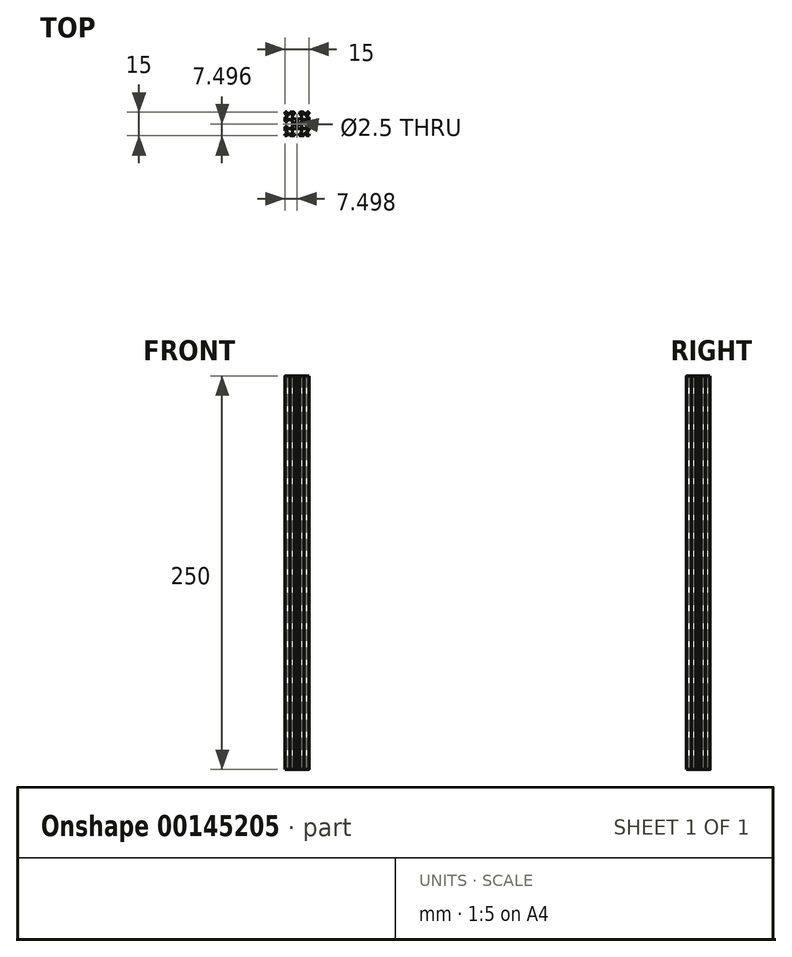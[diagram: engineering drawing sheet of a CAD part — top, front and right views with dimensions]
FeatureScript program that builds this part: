
annotation { "Feature Type Name" : "Feature", "Feature Type Description" : "" }
export const myFeature = defineFeature(function(context is Context, id is Id, definition is map)
    precondition{}
    {
        {
            var Q0;
            Q0=qCreatedBy(makeId("Top.planeOp"),FACE);
            var sketch = newSketch(context, id + "F0", { "sketchPlane" : qUnion([Q0])});
            skCircle(sketch, "E0", {"center": v(-4.16, 17.74) * mm, "radius": 1.25 * mm});
            skArc(sketch, "E1", {"start": v(-3.34, 15.19) * mm, "mid": v(-3.4, 15.33) * mm, "end": v(-3.54, 15.39) * mm});
            skLineSegment(sketch, "E2", {"start": v(-3.54, 15.39) * mm, "end": v(-4.79, 15.39) * mm});
            skArc(sketch, "E3", {"start": v(-4.79, 15.39) * mm, "mid": v(-4.93, 15.33) * mm, "end": v(-4.99, 15.19) * mm});
            skLineSegment(sketch, "E4", {"start": v(-4.99, 15.19) * mm, "end": v(-4.99, 14.96) * mm});
            skArc(sketch, "E5", {"start": v(-5.14, 14.77) * mm, "mid": v(-5.03, 14.84) * mm, "end": v(-4.99, 14.96) * mm});
            skLineSegment(sketch, "E6", {"start": v(-5.14, 14.77) * mm, "end": v(-6.67, 14.42) * mm});
            skArc(sketch, "E7", {"start": v(-6.67, 14.42) * mm, "mid": v(-6.95, 14.25) * mm, "end": v(-7.06, 13.94) * mm});
            skLineSegment(sketch, "E8", {"start": v(-7.06, 13.94) * mm, "end": v(-7.06, 11.84) * mm});
            skArc(sketch, "E9", {"start": v(-7.06, 11.84) * mm, "mid": v(-7, 11.7) * mm, "end": v(-6.86, 11.64) * mm});
            skLineSegment(sketch, "E10", {"start": v(-6.86, 11.64) * mm, "end": v(-6.26, 11.64) * mm});
            skArc(sketch, "E11", {"start": v(-5.76, 11.14) * mm, "mid": v(-5.9, 11.49) * mm, "end": v(-6.26, 11.64) * mm});
            skLineSegment(sketch, "E12", {"start": v(-5.76, 11.14) * mm, "end": v(-5.76, 10.74) * mm});
            skArc(sketch, "E13", {"start": v(-6.26, 10.24) * mm, "mid": v(-5.9, 10.38) * mm, "end": v(-5.76, 10.74) * mm});
            skArc(sketch, "E14", {"start": v(-8.56, 10.74) * mm, "mid": v(-8.42, 10.38) * mm, "end": v(-8.06, 10.24) * mm});
            skLineSegment(sketch, "E15", {"start": v(-8.56, 10.74) * mm, "end": v(-8.56, 11.07) * mm});
            skArc(sketch, "E16", {"start": v(-8.56, 11.07) * mm, "mid": v(-8.87, 11.53) * mm, "end": v(-9.42, 11.42) * mm});
            skLineSegment(sketch, "E17", {"start": v(-9.42, 11.42) * mm, "end": v(-10.45, 10.38) * mm});
            skArc(sketch, "E18", {"start": v(-10.8, 10.24) * mm, "mid": v(-10.62, 10.27) * mm, "end": v(-10.45, 10.38) * mm});
            skArc(sketch, "E19", {"start": v(-11.66, 10.49) * mm, "mid": v(-11.59, 10.3) * mm, "end": v(-11.41, 10.24) * mm});
            skArc(sketch, "E20", {"start": v(-11.52, 11.44) * mm, "mid": v(-11.62, 11.28) * mm, "end": v(-11.66, 11.09) * mm});
            skLineSegment(sketch, "E21", {"start": v(-11.52, 11.44) * mm, "end": v(-10.48, 12.48) * mm});
            skArc(sketch, "E22", {"start": v(-10.48, 12.48) * mm, "mid": v(-10.37, 13.03) * mm, "end": v(-10.83, 13.34) * mm});
            skLineSegment(sketch, "E23", {"start": v(-10.83, 13.34) * mm, "end": v(-11.16, 13.34) * mm});
            skArc(sketch, "E24", {"start": v(-11.66, 13.84) * mm, "mid": v(-11.52, 13.48) * mm, "end": v(-11.16, 13.34) * mm});
            skLineSegment(sketch, "E25", {"start": v(-11.66, 15.64) * mm, "end": v(-11.66, 13.84) * mm});
            skArc(sketch, "E26", {"start": v(-11.16, 16.14) * mm, "mid": v(-11.52, 15.99) * mm, "end": v(-11.66, 15.64) * mm});
            skLineSegment(sketch, "E27", {"start": v(-11.16, 16.14) * mm, "end": v(-10.76, 16.14) * mm});
            skArc(sketch, "E28", {"start": v(-10.26, 15.64) * mm, "mid": v(-10.4, 15.99) * mm, "end": v(-10.76, 16.14) * mm});
            skLineSegment(sketch, "E29", {"start": v(-10.26, 15.64) * mm, "end": v(-10.26, 15.04) * mm});
            skArc(sketch, "E30", {"start": v(-10.26, 15.04) * mm, "mid": v(-10.2, 14.9) * mm, "end": v(-10.06, 14.84) * mm});
            skLineSegment(sketch, "E31", {"start": v(-10.06, 14.84) * mm, "end": v(-7.96, 14.84) * mm});
            skArc(sketch, "E32", {"start": v(-7.96, 14.84) * mm, "mid": v(-7.65, 14.95) * mm, "end": v(-7.47, 15.23) * mm});
            skLineSegment(sketch, "E33", {"start": v(-7.47, 15.23) * mm, "end": v(-7.13, 16.75) * mm});
            skArc(sketch, "E34", {"start": v(-6.94, 16.91) * mm, "mid": v(-7.06, 16.87) * mm, "end": v(-7.13, 16.75) * mm});
            skLineSegment(sketch, "E35", {"start": v(-6.94, 16.91) * mm, "end": v(-6.7, 16.91) * mm});
            skArc(sketch, "E36", {"start": v(-6.7, 16.91) * mm, "mid": v(-6.57, 16.97) * mm, "end": v(-6.5, 17.11) * mm});
            skLineSegment(sketch, "E37", {"start": v(-6.5, 17.11) * mm, "end": v(-6.5, 18.36) * mm});
            skArc(sketch, "E38", {"start": v(-6.5, 18.36) * mm, "mid": v(-6.57, 18.5) * mm, "end": v(-6.7, 18.56) * mm});
            skLineSegment(sketch, "E39", {"start": v(-6.7, 18.56) * mm, "end": v(-6.94, 18.56) * mm});
            skArc(sketch, "E40", {"start": v(-7.13, 18.72) * mm, "mid": v(-7.06, 18.6) * mm, "end": v(-6.94, 18.56) * mm});
            skLineSegment(sketch, "E41", {"start": v(-7.13, 18.72) * mm, "end": v(-7.47, 20.25) * mm});
            skArc(sketch, "E42", {"start": v(-7.47, 20.25) * mm, "mid": v(-7.65, 20.53) * mm, "end": v(-7.96, 20.64) * mm});
            skLineSegment(sketch, "E43", {"start": v(-7.96, 20.64) * mm, "end": v(-10.06, 20.64) * mm});
            skArc(sketch, "E44", {"start": v(-10.06, 20.64) * mm, "mid": v(-10.2, 20.58) * mm, "end": v(-10.26, 20.44) * mm});
            skLineSegment(sketch, "E45", {"start": v(-10.26, 20.44) * mm, "end": v(-10.26, 19.84) * mm});
            skArc(sketch, "E46", {"start": v(-10.76, 19.34) * mm, "mid": v(-10.4, 19.48) * mm, "end": v(-10.26, 19.84) * mm});
            skLineSegment(sketch, "E47", {"start": v(-10.76, 19.34) * mm, "end": v(-11.16, 19.34) * mm});
            skArc(sketch, "E48", {"start": v(-11.66, 19.84) * mm, "mid": v(-11.52, 19.48) * mm, "end": v(-11.16, 19.34) * mm});
            skArc(sketch, "E49", {"start": v(-11.16, 22.14) * mm, "mid": v(-11.52, 21.99) * mm, "end": v(-11.66, 21.64) * mm});
            skLineSegment(sketch, "E50", {"start": v(-11.16, 22.14) * mm, "end": v(-10.83, 22.14) * mm});
            skArc(sketch, "E51", {"start": v(-10.83, 22.14) * mm, "mid": v(-10.37, 22.44) * mm, "end": v(-10.48, 22.99) * mm});
            skLineSegment(sketch, "E52", {"start": v(-10.48, 22.99) * mm, "end": v(-11.52, 24.03) * mm});
            skArc(sketch, "E53", {"start": v(-11.66, 24.38) * mm, "mid": v(-11.62, 24.2) * mm, "end": v(-11.52, 24.03) * mm});
            skArc(sketch, "E54", {"start": v(-11.41, 25.24) * mm, "mid": v(-11.59, 25.16) * mm, "end": v(-11.66, 24.99) * mm});
            skArc(sketch, "E55", {"start": v(-10.45, 25.09) * mm, "mid": v(-10.62, 25.2) * mm, "end": v(-10.8, 25.24) * mm});
            skLineSegment(sketch, "E56", {"start": v(-10.45, 25.09) * mm, "end": v(-9.42, 24.05) * mm});
            skArc(sketch, "E57", {"start": v(-9.42, 24.05) * mm, "mid": v(-8.87, 23.94) * mm, "end": v(-8.56, 24.4) * mm});
            skLineSegment(sketch, "E58", {"start": v(-8.56, 24.4) * mm, "end": v(-8.56, 24.74) * mm});
            skArc(sketch, "E59", {"start": v(-8.06, 25.24) * mm, "mid": v(-8.42, 25.09) * mm, "end": v(-8.56, 24.74) * mm});
            skArc(sketch, "E60", {"start": v(-5.76, 24.74) * mm, "mid": v(-5.9, 25.09) * mm, "end": v(-6.26, 25.24) * mm});
            skLineSegment(sketch, "E61", {"start": v(-5.76, 24.74) * mm, "end": v(-5.76, 24.34) * mm});
            skArc(sketch, "E62", {"start": v(-6.26, 23.84) * mm, "mid": v(-5.9, 23.98) * mm, "end": v(-5.76, 24.34) * mm});
            skLineSegment(sketch, "E63", {"start": v(-6.26, 23.84) * mm, "end": v(-6.86, 23.84) * mm});
            skArc(sketch, "E64", {"start": v(-6.86, 23.84) * mm, "mid": v(-7, 23.78) * mm, "end": v(-7.06, 23.64) * mm});
            skLineSegment(sketch, "E65", {"start": v(-7.06, 23.64) * mm, "end": v(-7.06, 21.54) * mm});
            skArc(sketch, "E66", {"start": v(-7.06, 21.54) * mm, "mid": v(-6.95, 21.22) * mm, "end": v(-6.67, 21.05) * mm});
            skLineSegment(sketch, "E67", {"start": v(-6.67, 21.05) * mm, "end": v(-5.14, 20.7) * mm});
            skArc(sketch, "E68", {"start": v(-4.99, 20.51) * mm, "mid": v(-5.03, 20.64) * mm, "end": v(-5.14, 20.7) * mm});
            skLineSegment(sketch, "E69", {"start": v(-4.99, 20.51) * mm, "end": v(-4.99, 20.28) * mm});
            skArc(sketch, "E70", {"start": v(-4.99, 20.28) * mm, "mid": v(-4.93, 20.14) * mm, "end": v(-4.79, 20.08) * mm});
            skLineSegment(sketch, "E71", {"start": v(-4.79, 20.08) * mm, "end": v(-3.54, 20.08) * mm});
            skArc(sketch, "E72", {"start": v(-3.54, 20.08) * mm, "mid": v(-3.4, 20.14) * mm, "end": v(-3.34, 20.28) * mm});
            skLineSegment(sketch, "E73", {"start": v(-3.34, 20.28) * mm, "end": v(-3.34, 20.51) * mm});
            skArc(sketch, "E74", {"start": v(-3.18, 20.7) * mm, "mid": v(-3.3, 20.64) * mm, "end": v(-3.34, 20.51) * mm});
            skLineSegment(sketch, "E75", {"start": v(-3.18, 20.7) * mm, "end": v(-1.65, 21.05) * mm});
            skArc(sketch, "E76", {"start": v(-1.65, 21.05) * mm, "mid": v(-1.37, 21.22) * mm, "end": v(-1.26, 21.54) * mm});
            skLineSegment(sketch, "E77", {"start": v(-1.26, 21.54) * mm, "end": v(-1.26, 23.64) * mm});
            skArc(sketch, "E78", {"start": v(-1.26, 23.64) * mm, "mid": v(-1.32, 23.78) * mm, "end": v(-1.46, 23.84) * mm});
            skLineSegment(sketch, "E79", {"start": v(-1.46, 23.84) * mm, "end": v(-2.06, 23.84) * mm});
            skArc(sketch, "E80", {"start": v(-2.56, 24.34) * mm, "mid": v(-2.42, 23.98) * mm, "end": v(-2.06, 23.84) * mm});
            skLineSegment(sketch, "E81", {"start": v(-2.56, 24.34) * mm, "end": v(-2.56, 24.74) * mm});
            skArc(sketch, "E82", {"start": v(-2.06, 25.24) * mm, "mid": v(-2.42, 25.09) * mm, "end": v(-2.56, 24.74) * mm});
            skArc(sketch, "E83", {"start": v(0.24, 24.74) * mm, "mid": v(0.1, 25.09) * mm, "end": v(-0.26, 25.24) * mm});
            skLineSegment(sketch, "E84", {"start": v(0.24, 24.74) * mm, "end": v(0.24, 24.4) * mm});
            skArc(sketch, "E85", {"start": v(0.24, 24.4) * mm, "mid": v(0.55, 23.94) * mm, "end": v(1.1, 24.05) * mm});
            skLineSegment(sketch, "E86", {"start": v(1.1, 24.05) * mm, "end": v(2.13, 25.09) * mm});
            skArc(sketch, "E87", {"start": v(2.48, 25.24) * mm, "mid": v(2.3, 25.2) * mm, "end": v(2.13, 25.09) * mm});
            skLineSegment(sketch, "E88", {"start": v(3.09, 25.24) * mm, "end": v(2.48, 25.24) * mm});
            skArc(sketch, "E89", {"start": v(3.34, 24.99) * mm, "mid": v(3.27, 25.16) * mm, "end": v(3.09, 25.24) * mm});
            skArc(sketch, "E90", {"start": v(3.2, 24.03) * mm, "mid": v(3.3, 24.2) * mm, "end": v(3.34, 24.38) * mm});
            skLineSegment(sketch, "E91", {"start": v(3.2, 24.03) * mm, "end": v(2.15, 22.99) * mm});
            skArc(sketch, "E92", {"start": v(2.15, 22.99) * mm, "mid": v(2.04, 22.44) * mm, "end": v(2.5, 22.14) * mm});
            skLineSegment(sketch, "E93", {"start": v(2.5, 22.14) * mm, "end": v(2.84, 22.14) * mm});
            skArc(sketch, "E94", {"start": v(3.34, 21.64) * mm, "mid": v(3.2, 21.99) * mm, "end": v(2.84, 22.14) * mm});
            skArc(sketch, "E95", {"start": v(2.84, 19.34) * mm, "mid": v(3.2, 19.48) * mm, "end": v(3.34, 19.84) * mm});
            skLineSegment(sketch, "E96", {"start": v(2.84, 19.34) * mm, "end": v(2.44, 19.34) * mm});
            skArc(sketch, "E97", {"start": v(1.94, 19.84) * mm, "mid": v(2.08, 19.48) * mm, "end": v(2.44, 19.34) * mm});
            skLineSegment(sketch, "E98", {"start": v(1.94, 19.84) * mm, "end": v(1.94, 20.44) * mm});
            skArc(sketch, "E99", {"start": v(1.94, 20.44) * mm, "mid": v(1.88, 20.58) * mm, "end": v(1.74, 20.64) * mm});
            skLineSegment(sketch, "E100", {"start": v(1.74, 20.64) * mm, "end": v(-0.36, 20.64) * mm});
            skArc(sketch, "E101", {"start": v(-0.36, 20.64) * mm, "mid": v(-0.67, 20.53) * mm, "end": v(-0.85, 20.25) * mm});
            skLineSegment(sketch, "E102", {"start": v(-0.85, 20.25) * mm, "end": v(-1.2, 18.72) * mm});
            skArc(sketch, "E103", {"start": v(-1.39, 18.56) * mm, "mid": v(-1.26, 18.6) * mm, "end": v(-1.2, 18.72) * mm});
            skLineSegment(sketch, "E104", {"start": v(-1.39, 18.56) * mm, "end": v(-1.61, 18.56) * mm});
            skArc(sketch, "E105", {"start": v(-1.61, 18.56) * mm, "mid": v(-1.76, 18.5) * mm, "end": v(-1.81, 18.36) * mm});
            skLineSegment(sketch, "E106", {"start": v(-1.81, 18.36) * mm, "end": v(-1.81, 17.11) * mm});
            skArc(sketch, "E107", {"start": v(-1.81, 17.11) * mm, "mid": v(-1.76, 16.97) * mm, "end": v(-1.61, 16.91) * mm});
            skLineSegment(sketch, "E108", {"start": v(-1.61, 16.91) * mm, "end": v(-1.39, 16.91) * mm});
            skArc(sketch, "E109", {"start": v(-1.2, 16.75) * mm, "mid": v(-1.26, 16.87) * mm, "end": v(-1.39, 16.91) * mm});
            skLineSegment(sketch, "E110", {"start": v(-1.2, 16.75) * mm, "end": v(-0.85, 15.23) * mm});
            skArc(sketch, "E111", {"start": v(-0.85, 15.23) * mm, "mid": v(-0.67, 14.95) * mm, "end": v(-0.36, 14.84) * mm});
            skLineSegment(sketch, "E112", {"start": v(-0.36, 14.84) * mm, "end": v(1.74, 14.84) * mm});
            skArc(sketch, "E113", {"start": v(1.74, 14.84) * mm, "mid": v(1.88, 14.9) * mm, "end": v(1.94, 15.04) * mm});
            skLineSegment(sketch, "E114", {"start": v(1.94, 15.04) * mm, "end": v(1.94, 15.64) * mm});
            skArc(sketch, "E115", {"start": v(2.44, 16.14) * mm, "mid": v(2.08, 15.99) * mm, "end": v(1.94, 15.64) * mm});
            skLineSegment(sketch, "E116", {"start": v(2.44, 16.14) * mm, "end": v(2.84, 16.14) * mm});
            skArc(sketch, "E117", {"start": v(3.34, 15.64) * mm, "mid": v(3.2, 15.99) * mm, "end": v(2.84, 16.14) * mm});
            skLineSegment(sketch, "E118", {"start": v(3.34, 13.84) * mm, "end": v(3.34, 15.64) * mm});
            skArc(sketch, "E119", {"start": v(2.84, 13.34) * mm, "mid": v(3.2, 13.48) * mm, "end": v(3.34, 13.84) * mm});
            skLineSegment(sketch, "E120", {"start": v(2.84, 13.34) * mm, "end": v(2.5, 13.34) * mm});
            skArc(sketch, "E121", {"start": v(2.5, 13.34) * mm, "mid": v(2.04, 13.03) * mm, "end": v(2.15, 12.48) * mm});
            skLineSegment(sketch, "E122", {"start": v(2.15, 12.48) * mm, "end": v(3.2, 11.44) * mm});
            skArc(sketch, "E123", {"start": v(3.34, 11.09) * mm, "mid": v(3.3, 11.28) * mm, "end": v(3.2, 11.44) * mm});
            skArc(sketch, "E124", {"start": v(3.09, 10.24) * mm, "mid": v(3.27, 10.3) * mm, "end": v(3.34, 10.49) * mm});
            skLineSegment(sketch, "E125", {"start": v(2.48, 10.24) * mm, "end": v(3.09, 10.24) * mm});
            skArc(sketch, "E126", {"start": v(2.13, 10.38) * mm, "mid": v(2.3, 10.27) * mm, "end": v(2.48, 10.24) * mm});
            skLineSegment(sketch, "E127", {"start": v(2.13, 10.38) * mm, "end": v(1.1, 11.42) * mm});
            skArc(sketch, "E128", {"start": v(1.1, 11.42) * mm, "mid": v(0.55, 11.53) * mm, "end": v(0.24, 11.07) * mm});
            skLineSegment(sketch, "E129", {"start": v(0.24, 11.07) * mm, "end": v(0.24, 10.74) * mm});
            skArc(sketch, "E130", {"start": v(-0.26, 10.24) * mm, "mid": v(0.1, 10.38) * mm, "end": v(0.24, 10.74) * mm});
            skArc(sketch, "E131", {"start": v(-2.56, 10.74) * mm, "mid": v(-2.42, 10.38) * mm, "end": v(-2.06, 10.24) * mm});
            skLineSegment(sketch, "E132", {"start": v(-2.56, 10.74) * mm, "end": v(-2.56, 11.14) * mm});
            skArc(sketch, "E133", {"start": v(-2.06, 11.64) * mm, "mid": v(-2.42, 11.49) * mm, "end": v(-2.56, 11.14) * mm});
            skLineSegment(sketch, "E134", {"start": v(-2.06, 11.64) * mm, "end": v(-1.46, 11.64) * mm});
            skArc(sketch, "E135", {"start": v(-1.46, 11.64) * mm, "mid": v(-1.32, 11.7) * mm, "end": v(-1.26, 11.84) * mm});
            skLineSegment(sketch, "E136", {"start": v(-1.26, 11.84) * mm, "end": v(-1.26, 13.94) * mm});
            skArc(sketch, "E137", {"start": v(-1.26, 13.94) * mm, "mid": v(-1.37, 14.25) * mm, "end": v(-1.65, 14.42) * mm});
            skLineSegment(sketch, "E138", {"start": v(-1.65, 14.42) * mm, "end": v(-3.18, 14.77) * mm});
            skArc(sketch, "E139", {"start": v(-3.34, 14.96) * mm, "mid": v(-3.3, 14.84) * mm, "end": v(-3.18, 14.77) * mm});
            skLineSegment(sketch, "E140", {"start": v(-3.34, 14.96) * mm, "end": v(-3.34, 15.19) * mm});
            skLineSegment(sketch, "E141", {"start": v(-11.66, 21.64) * mm, "end": v(-11.66, 19.84) * mm});
            skLineSegment(sketch, "E142", {"start": v(-10.8, 25.24) * mm, "end": v(-11.41, 25.24) * mm});
            skLineSegment(sketch, "E143", {"start": v(-8.06, 10.24) * mm, "end": v(-6.26, 10.24) * mm});
            skLineSegment(sketch, "E144", {"start": v(3.34, 19.84) * mm, "end": v(3.34, 21.64) * mm});
            skLineSegment(sketch, "E145", {"start": v(-11.66, 24.99) * mm, "end": v(-11.66, 24.38) * mm});
            skLineSegment(sketch, "E146", {"start": v(3.34, 10.49) * mm, "end": v(3.34, 11.09) * mm});
            skLineSegment(sketch, "E147", {"start": v(3.34, 24.38) * mm, "end": v(3.34, 24.99) * mm});
            skLineSegment(sketch, "E148", {"start": v(-6.26, 25.24) * mm, "end": v(-8.06, 25.24) * mm});
            skLineSegment(sketch, "E149", {"start": v(-11.66, 11.09) * mm, "end": v(-11.66, 10.49) * mm});
            skLineSegment(sketch, "E150", {"start": v(-0.26, 25.24) * mm, "end": v(-2.06, 25.24) * mm});
            skLineSegment(sketch, "E151", {"start": v(-2.06, 10.24) * mm, "end": v(-0.26, 10.24) * mm});
            skLineSegment(sketch, "E152", {"start": v(-11.41, 10.24) * mm, "end": v(-10.8, 10.24) * mm});
            skLineSegment(sketch, "E153", {"start": v(-4.16, 17.74) * mm, "end": v(-4.16, 20.24) * mm});
            skLineSegment(sketch, "E154", {"start": v(-4.16, 17.74) * mm, "end": v(-6.66, 17.74) * mm});
            skLineSegment(sketch, "E155", {"start": v(-4.16, 17.74) * mm, "end": v(-4.16, 15.24) * mm});
            skLineSegment(sketch, "E156", {"start": v(-4.16, 17.74) * mm, "end": v(-1.66, 17.74) * mm});
            skLineSegment(sketch, "E157", {"start": v(-4.16, 20.24) * mm, "end": v(-4.16, 21.49) * mm});
            skLineSegment(sketch, "E158", {"start": v(-6.66, 17.74) * mm, "end": v(-7.91, 17.74) * mm});
            skLineSegment(sketch, "E159", {"start": v(-4.16, 15.24) * mm, "end": v(-4.16, 13.99) * mm});
            skLineSegment(sketch, "E160", {"start": v(-1.66, 17.74) * mm, "end": v(-0.41, 17.74) * mm});
            skSolve(sketch);
        }
        {
            var Q0;
            Q0=qSketchRegion(id+"F0",true);
            var Q1;
            {var subQ5=sQuery(id+"F0.wireOp",EDGE,"E3");Q1=makeQuery(id+"F0.imprint","IMPRINT",FACE,{"disambiguationData":[TD([[makeQuery(id+"F0.imprint","IMPRINT",EDGE,{"derivedFrom":subQ5}),-1.0]])]});}
            var Q2;
            {var subQ0=sQuery(id+"F0.wireOp",EDGE,"E38");Q2=makeQuery(id+"F0.imprint","IMPRINT",FACE,{"disambiguationData":[TD([[makeQuery(id+"F0.imprint","IMPRINT",EDGE,{"derivedFrom":subQ0}),-1.0]])]});}
            var Q3;
            {var subQ7=sQuery(id+"F0.wireOp",EDGE,"E72");Q3=makeQuery(id+"F0.imprint","IMPRINT",FACE,{"disambiguationData":[TD([[makeQuery(id+"F0.imprint","IMPRINT",EDGE,{"derivedFrom":subQ7}),-1.0]])]});}
            extrude(context, id + "F1", {"entities" : qUnion([Q0, Q1, Q2, Q3]), "depth" : 250 * mm});
        }
    });
